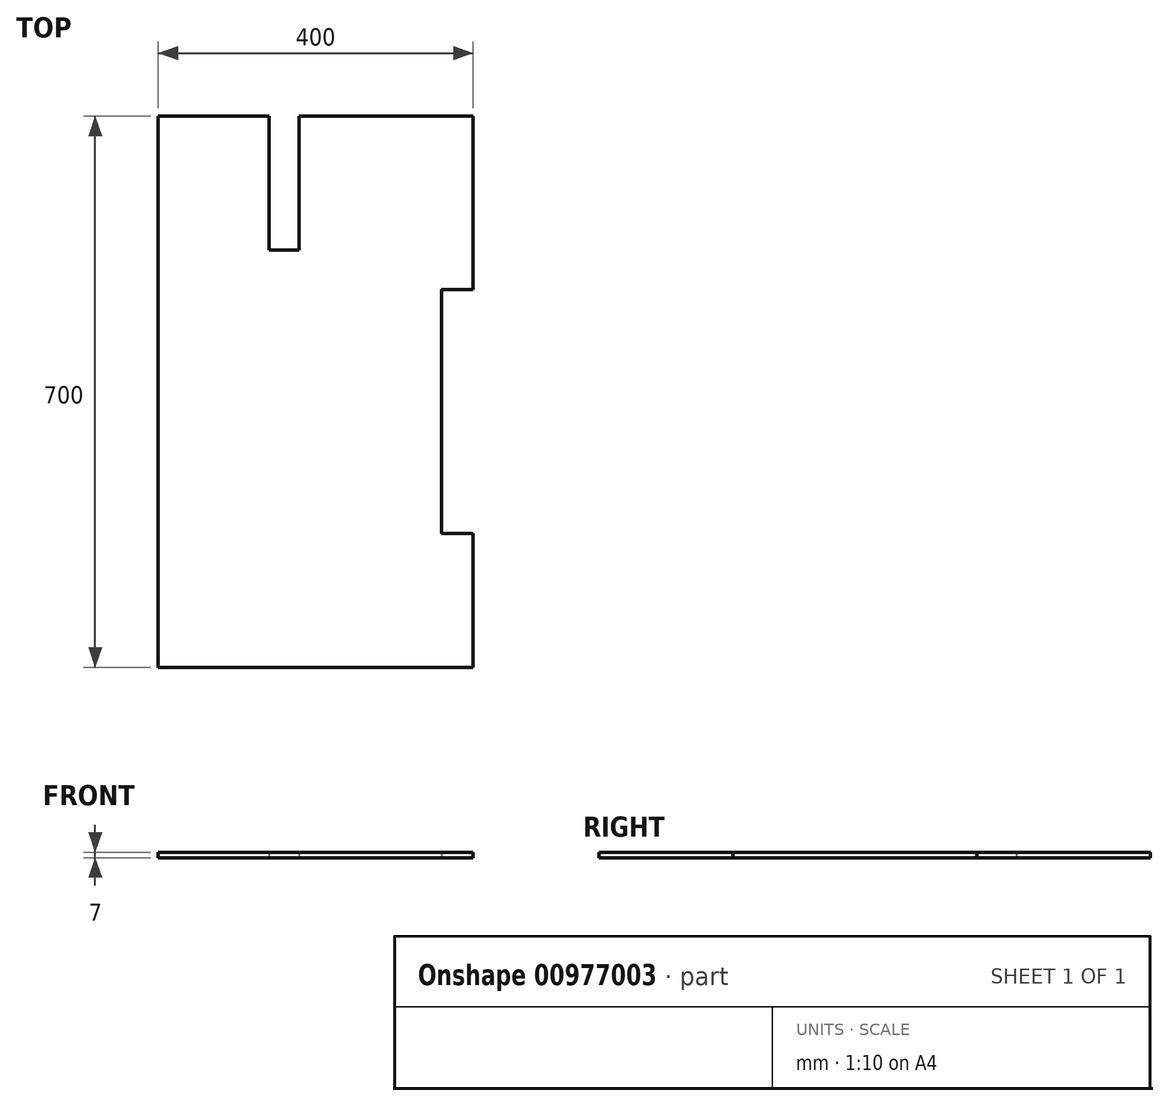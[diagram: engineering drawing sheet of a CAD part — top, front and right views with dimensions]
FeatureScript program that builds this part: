
annotation { "Feature Type Name" : "Feature", "Feature Type Description" : "" }
export const myFeature = defineFeature(function(context is Context, id is Id, definition is map)
    precondition{}
    {
        {
            var Q0;
            Q0=qCreatedBy(makeId("Top.planeOp"),FACE);
            var sketch = newSketch(context, id + "F0", { "sketchPlane" : qUnion([Q0])});
            skLineSegment(sketch, "E0.bottom", {"start": v(0, 0) * mm, "end": v(140.5, 0) * mm});
            skLineSegment(sketch, "E0.top", {"start": v(0, -700) * mm, "end": v(400, -700) * mm});
            skLineSegment(sketch, "E0.left", {"start": v(0, 0) * mm, "end": v(0, -700) * mm});
            skLineSegment(sketch, "E0.right", {"start": v(400, 0) * mm, "end": v(400, -220) * mm});
            skLineSegment(sketch, "E1.bottom", {"start": v(140.5, -170) * mm, "end": v(179.2, -170) * mm});
            skLineSegment(sketch, "E1.left", {"start": v(140.5, 0) * mm, "end": v(140.5, -170) * mm});
            skLineSegment(sketch, "E1.right", {"start": v(179.2, 0) * mm, "end": v(179.2, -170) * mm});
            skLineSegment(sketch, "E2", {"start": v(179.2, 0) * mm, "end": v(179.2, -85) * mm, "construction": true});
            skLineSegment(sketch, "E3.trimOffspring", {"start": v(179.2, 0) * mm, "end": v(400, 0) * mm});
            skLineSegment(sketch, "E4", {"start": v(400, -220) * mm, "end": v(360.2, -220) * mm});
            skLineSegment(sketch, "E5", {"start": v(360.2, -220) * mm, "end": v(360.2, -530) * mm});
            skLineSegment(sketch, "E6", {"start": v(360.2, -530) * mm, "end": v(400, -530) * mm});
            skLineSegment(sketch, "E7", {"start": v(400, -220) * mm, "end": v(400, -530) * mm, "construction": true});
            skLineSegment(sketch, "E8", {"start": v(400, -530) * mm, "end": v(400, -700) * mm});
            skSolve(sketch);
        }
        {
            var Q0;
            Q0=makeQuery(id+"F0.imprint","IMPRINT",FACE,{"disambiguationData":[TD([[makeQuery(id+"F0.imprint","IMPRINT",EDGE,{"derivedFrom":sQuery(id+"F0.wireOp",EDGE,"E0.bottom")}),-1.0]])]});
            extrude(context, id + "F1", {"entities" : qUnion([Q0]), "depth" : 7 * mm, "offsetDistance" : 25 * mm});
        }
    });
